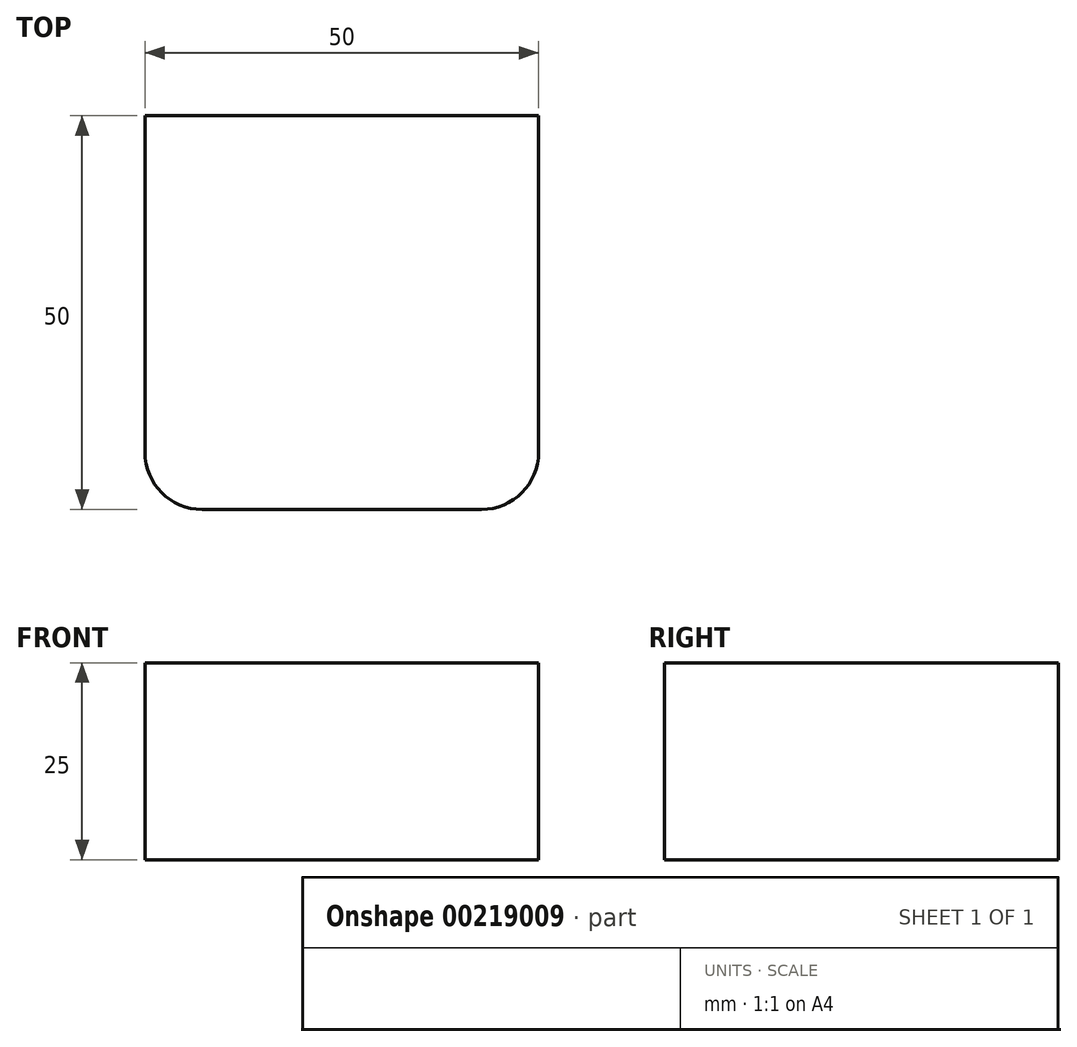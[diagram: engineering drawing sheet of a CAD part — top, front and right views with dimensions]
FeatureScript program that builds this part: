
annotation { "Feature Type Name" : "Feature", "Feature Type Description" : "" }
export const myFeature = defineFeature(function(context is Context, id is Id, definition is map)
    precondition{}
    {
        {
            var Q0;
            Q0=qCreatedBy(makeId("Top.planeOp"),FACE);
            var sketch = newSketch(context, id + "F0", { "sketchPlane" : qUnion([Q0])});
            skLineSegment(sketch, "E0.bottom", {"start": v(0, 0) * mm, "end": v(50, 0) * mm});
            skLineSegment(sketch, "E0.top", {"start": v(0, 50) * mm, "end": v(50, 50) * mm});
            skLineSegment(sketch, "E0.left", {"start": v(0, 0) * mm, "end": v(0, 50) * mm});
            skLineSegment(sketch, "E0.right", {"start": v(50, 0) * mm, "end": v(50, 50) * mm});
            skSolve(sketch);
        }
        {
            var Q0;
            Q0=makeQuery(id+"F0.imprint","IMPRINT",FACE,{"disambiguationData":[TD([[makeQuery(id+"F0.imprint","IMPRINT",EDGE,{"derivedFrom":sQuery(id+"F0.wireOp",EDGE,"E0.bottom")}),1.0]])]});
            extrude(context, id + "F1", {"entities" : qUnion([Q0]), "depth" : 25 * mm});
        }
        {
            var Q0;
            Q0=makeQuery(id+"F1.opExtrude","SWEPT_EDGE",EDGE,{"disambiguationData":[OSD([sQuery(id+"F0.wireOp",EDGE,"E0.bottom"),sQuery(id+"F0.wireOp",EDGE,"E0.left")])]});
            var Q1;
            Q1=makeQuery(id+"F1.opExtrude","SWEPT_EDGE",EDGE,{"disambiguationData":[OSD([sQuery(id+"F0.wireOp",EDGE,"E0.bottom"),sQuery(id+"F0.wireOp",EDGE,"E0.right")])]});
            fillet(context, id + "F2", {"entities" : qUnion([Q0, Q1]), "radius" : 7.24 * mm, "tangentPropagation" : true, "allowEdgeOverflow" : false});
        }
    });
